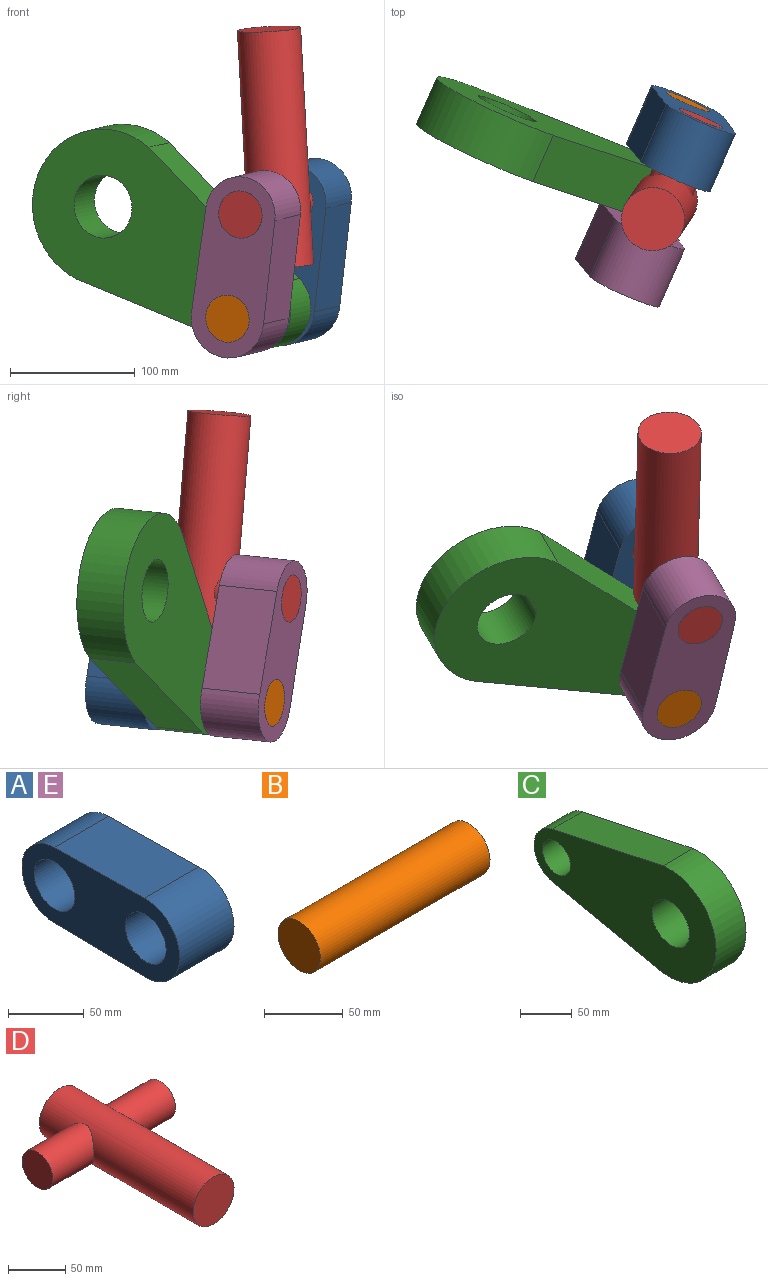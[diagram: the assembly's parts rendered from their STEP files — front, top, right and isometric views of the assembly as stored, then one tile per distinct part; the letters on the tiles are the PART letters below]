
ASSEMBLY  parts=5 mates=5
PART A: 8 faces, bbox 50.8x147.5x63.5 mm
  f0: cylinder r=30.48mm len=60.95mm, axis (-1,0,0), area 4818.6mm2, adj f1,f3,f6,f7
  f1: plane 84.59x50.8mm, normal (0,0.01,1), area 4297.8mm2, adj f0,f2,f6,f7
  f2: cylinder r=31.75mm len=63.5mm, axis (-1,0,0), area 5187.3mm2, adj f1,f3,f6,f7
  f3: plane 84.51x50.8mm, normal (0,0.01,-1), area 4293.8mm2, adj f0,f2,f6,f7
  f4: cylinder r=19.05mm len=50.8mm, axis (-1,0,0), area 6080.5mm2, adj f6,f7
  f5: cylinder r=19.05mm len=50.8mm, axis (-1,0,0), area 6080.5mm2, adj f6,f7
  f6: plane 147.52x63.5mm, normal (1,0,0), area 6069.8mm2, adj f0,f1,f2,f3,f4,f5
  f7: plane 147.52x63.5mm, normal (-1,0,0), area 6069.8mm2, adj f0,f1,f2,f3,f4,f5
PART B: 3 faces, bbox 152.4x38.1x38.1 mm
  f0: cylinder r=19.05mm len=152.4mm, axis (-1,0,0), area 18241.5mm2, adj f1,f2
  f1: plane 38.1x38.1mm, normal (1,0,0), area 1140.1mm2, adj f0
  f2: plane 38.1x38.1mm, normal (-1,0,0), area 1140.1mm2, adj f0
PART C: 8 faces, bbox 40.7x247.7x127 mm
  f0: plane 150.47x40.65mm, normal (0,0.21,0.98), area 6252.2mm2, adj f1,f3,f4,f5
  f1: cylinder r=63.5mm len=127mm, axis (-1,0,0), area 8759.8mm2, adj f0,f2,f4,f5
  f2: plane 151.52x40.65mm, normal (0,0.21,-0.98), area 6295.2mm2, adj f1,f3,f4,f5
  f3: cylinder r=31.75mm len=62.13mm, axis (-1,0,0), area 3516.8mm2, adj f0,f2,f4,f5
  f4: plane 247.65x127mm, normal (1,0,0), area 19548.6mm2, adj f0,f1,f2,f3,f6,f7
  f5: plane 247.65x127mm, normal (-1,0,0), area 19548.6mm2, adj f0,f1,f2,f3,f6,f7
  f6: cylinder r=25.4mm len=50.8mm, axis (-1,0,0), area 6487.6mm2, adj f4,f5
  f7: cylinder r=19.05mm len=40.65mm, axis (-1,0,0), area 4865.7mm2, adj f4,f5
PART D: 7 faces, bbox 152.4x190.5x50.8 mm
  f0: cylinder r=25.4mm len=190.5mm, axis (0,1,0), area 27912.1mm2, adj f1,f2,f3,f5
  f1: plane 50.8x50.8mm, normal (0,-1,0), area 2026.8mm2, adj f0
  f2: plane 50.8x50.8mm, normal (0,1,0), area 2026.8mm2, adj f0
  f3: cylinder r=19.05mm len=59.4mm, axis (-1,0,0), area 6569.4mm2, adj f0,f4
  f4: plane 38.1x38.1mm, normal (1,0,0), area 1140.1mm2, adj f3
  f5: cylinder r=19.05mm len=59.4mm, axis (1,0,0), area 6568.2mm2, adj f0,f6
  f6: plane 38.1x38.1mm, normal (-1,0,0), area 1140.1mm2, adj f5
PART E: same geometry as A
PLACE A rot(axis=(0.77,0.46,0.45),117.7deg) t=(16.3,194.18,25.92)mm
PLACE B rot(axis=(0.77,0.46,0.45),117.7deg) t=(-30.52,109.42,-31.84)mm
PLACE C rot(axis=(-0.82,-0.55,0.12),149.4deg) t=(-56.04,177.97,6.74)mm
PLACE D rot(axis=(-0.73,-0.52,0.44),105.4deg) t=(13.11,169.28,11)mm
PLACE E rot(axis=(0.77,0.46,0.45),117.7deg) t=(-24.58,101.69,16.08)mm
MATE revolute B.f0 <-> A.f5  axis (0.4,0.91,0.1) through (30.8,248.15,-17.08)mm
MATE revolute B.f0 <-> C.f7  axis (-0.4,-0.91,-0.1) through (0.14,178.78,-24.46)mm
MATE revolute E.f4 <-> D.f3  axis (-0.4,-0.91,-0.1) through (-20.16,95.94,51.73)mm
MATE revolute A.f4 <-> D.f3  axis (-0.4,-0.91,-0.1) through (41.17,234.67,66.49)mm
MATE revolute B.f0 <-> E.f5  axis (-0.4,-0.91,-0.1) through (-30.52,109.42,-31.84)mm
